# Revit family: BOVER_FORA-90
name_source: partatom
category: Lighting Fixtures
units: mm (PartAtom-declared; Revit-internal decimal feet)

## family parameters
Cut with Voids When Loaded = No
Host = Face
Light Source = No
Part Type = Normal
Room Calculation Point = No
Round Connector Dimension = Use Diameter
Shared = No

## types (4) — shared parameters
BV_AssemblyInstructions_URL = https://www.bover.es
BV_CRI = 90
BV_IP-MedicalDevice = -
BV_Photometry_CE-USA_URL = https://www.bover.es
BV_SaleCountry = USA
BV_TechnicalURL = https://www.bover.es
D = 900 mm
Default Elevation = 1219.2 mm  [stored 4 ft]
Diffuser = Opal PVC
EditionNumber = 2
GubimclassCode = 50.60.50.20
GubimclassDescription = Iluminación interior
H = 2500 mm
IfcExportAs = IfcLightFixtureType
IfcExportType = NOTDEFINED
IssueDate = July 2021
Manufacturer = BOVER
Model = FORA
OmniclassCode = 23.35.47.00
OmniclassDescription = Electrical Lighting
URL = https://www.bover.es
Uniclass2015Code = Pr_70_70_48_46
Uniclass2015Description = Light-emitting diode (LED) luminaires
Uniformat2010Code = D5020200
Uniformat2010Description = Lighting Equipment
Version = RVT_19

## per-type parameters (varying)
| type | BV_Code | BV_EAN | BV_SpanishDescription | Body | Description | Shaded |
| FORA_90_LED_TRIAC_WHITE | 30302214128U | 8435493738659 | FORA 90 LED TRIAC BLANCO ROTO-BEIGE CLARO | 013_Graphite White | FORA 90 PENDANT - LED TRIAC NATURAL WHITE - LIGHT BEIGE | Light beige |
| FORA_90_LED_TRIAC_BROWN | 30302214127U | 8435493738642 | FORA 90 LED TRIAC MARRÓN GRAF-MARRÓN RATTAN | 014_Brown Graphite | FORA 90 PENDANT - LED TRIAC GRAPHITE BROWN - RATTAN BROWN | Rattan brown |
| FORA_90_LED_0-10V_WHITE | 30302204128U | 8435493734217 | FORA 90 LED 0-10V BLANCO ROTO-BEIGE CLARO | 013_Graphite White | FORA 90 PENDANT - LED 0-10V NATURAL WHITE - LIGHT BEIGE | Light beige |
| FORA_90_LED_0-10V_BROWN | 30302204127U | 8435493734200 | FORA 90 LED 0-10V MARRÓN GRAF-MARRÓN RATTAN | 014_Brown Graphite | FORA 90 PENDANT - LED 0-10V GRAPHITE BROWN - RATTAN BROWN | Rattan brown |

note: [stored X ft] marks values corroborated as IEEE doubles in the binary element streams (Revit-internal decimal feet)

## geometry (parser evidence)
native form markers: Blend x2
no freeform markers — native parametric forms only
